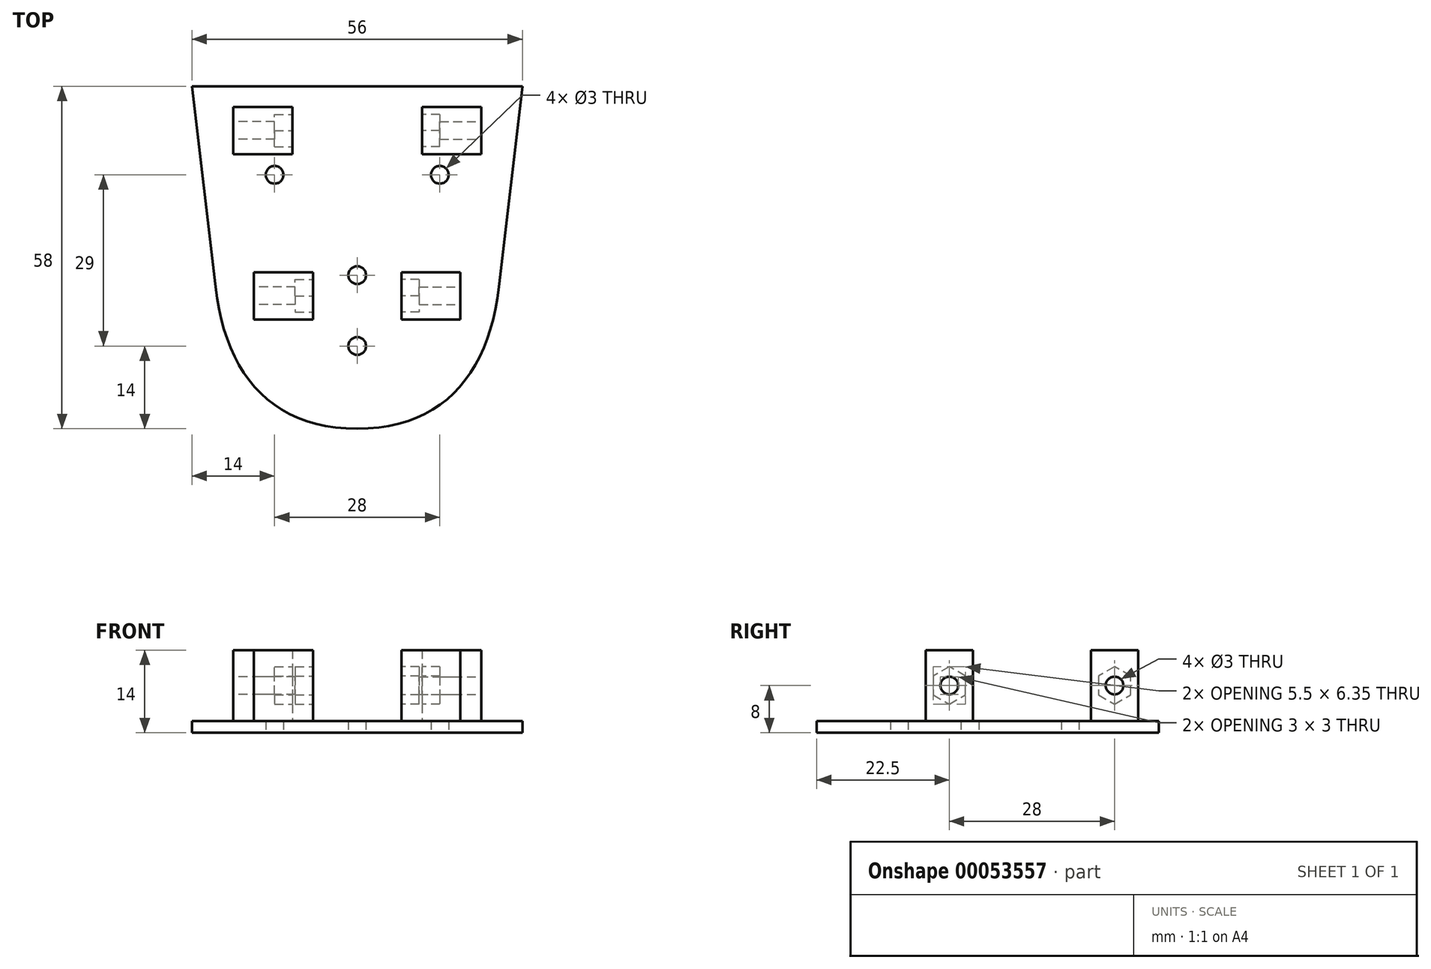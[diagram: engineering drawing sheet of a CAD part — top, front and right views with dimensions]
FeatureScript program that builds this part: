
annotation { "Feature Type Name" : "Feature", "Feature Type Description" : "" }
export const myFeature = defineFeature(function(context is Context, id is Id, definition is map)
    precondition{}
    {
        {
            var Q0;
            Q0=qCreatedBy(makeId("Top.planeOp"),FACE);
            var sketch = newSketch(context, id + "F0", { "sketchPlane" : qUnion([Q0])});
            skLineSegment(sketch, "E0.bottom", {"start": v(28, -29) * mm, "end": v(-28, -29) * mm, "construction": true});
            skLineSegment(sketch, "E0.top", {"start": v(28, 29) * mm, "end": v(-28, 29) * mm, "construction": true});
            skLineSegment(sketch, "E0.left", {"start": v(28, -29) * mm, "end": v(28, 29) * mm, "construction": true});
            skLineSegment(sketch, "E0.right", {"start": v(-28, -29) * mm, "end": v(-28, 29) * mm, "construction": true});
            skPoint(sketch, "E0.middle", {"position": v(0, 0) * mm});
            skLineSegment(sketch, "E1", {"start": v(-28, 14) * mm, "end": v(28, 14) * mm, "construction": true});
            skCircle(sketch, "E2", {"center": v(14, 14) * mm, "radius": 1.5 * mm});
            skCircle(sketch, "E3.MirrorC", {"center": v(-14, 14) * mm, "radius": 1.5 * mm});
            skCircle(sketch, "E4", {"center": v(0, -3) * mm, "radius": 1.5 * mm});
            skCircle(sketch, "E5", {"center": v(0, -15) * mm, "radius": 1.5 * mm});
            skLineSegment(sketch, "E6", {"start": v(-28, -5) * mm, "end": v(28, -5) * mm, "construction": true});
            skPoint(sketch, "E7", {"position": v(24, -5) * mm});
            skPoint(sketch, "E8.MirrorP", {"position": v(-24, -5) * mm});
            skLineSegment(sketch, "E9", {"start": v(28, 29) * mm, "end": v(24, -5) * mm});
            skFitSpline(sketch, "E10", {"points": [v(24, -5) * mm, v(0, -29) * mm], "startDerivative": vector(-5.06, -43.9) * mm, "endDerivative": vector(-43.96, 0) * mm});
            skFitSpline(sketch, "E11.MirrorCS", {"points": [v(-24, -5) * mm, v(0, -29) * mm], "startDerivative": vector(5.06, -43.9) * mm, "endDerivative": vector(43.96, 0) * mm});
            skLineSegment(sketch, "E12.MirrorCS", {"start": v(-28, 29) * mm, "end": v(-24, -5) * mm});
            skLineSegment(sketch, "E13", {"start": v(-28, 29) * mm, "end": v(28, 29) * mm});
            skSolve(sketch);
        }
        {
            var Q0;
            Q0 = qSketchRegion(id + "F0", true);
            extrude(context, id + "F1", {"entities" : qUnion([Q0]), "depth" : 2 * mm});
        }
        {
            var Q0;
            Q0=makeQuery(id+"F1.opExtrude","CAP_FACE",FACE,{"disambiguationData":[OSD([sQuery(id+"F0.wireOp",EDGE,"E2"),sQuery(id+"F0.wireOp",EDGE,"E3.MirrorC"),sQuery(id+"F0.wireOp",EDGE,"E4"),sQuery(id+"F0.wireOp",EDGE,"E5"),sQuery(id+"F0.wireOp",EDGE,"E9"),sQuery(id+"F0.wireOp",EDGE,"E10"),sQuery(id+"F0.wireOp",EDGE,"E11.MirrorCS"),sQuery(id+"F0.wireOp",EDGE,"E12.MirrorCS"),sQuery(id+"F0.wireOp",EDGE,"E13")])],"isStart":false});
            var sketch = newSketch(context, id + "F2", { "sketchPlane" : qUnion([Q0])});
            skLineSegment(sketch, "E14", {"start": v(-27.59, 25.5) * mm, "end": v(-21, 25.5) * mm, "construction": true});
            skLineSegment(sketch, "E15", {"start": v(21, 25.5) * mm, "end": v(21, -43.4) * mm, "construction": true});
            skLineSegment(sketch, "E16.bottom", {"start": v(11, 25.5) * mm, "end": v(21, 25.5) * mm});
            skLineSegment(sketch, "E16.top", {"start": v(11, 17.5) * mm, "end": v(21, 17.5) * mm});
            skLineSegment(sketch, "E16.left", {"start": v(11, 25.5) * mm, "end": v(11, 17.5) * mm});
            skLineSegment(sketch, "E16.right", {"start": v(21, 25.5) * mm, "end": v(21, 17.5) * mm});
            skLineSegment(sketch, "E17", {"start": v(17.5, -30.53) * mm, "end": v(17.5, 35.38) * mm, "construction": true});
            skLineSegment(sketch, "E18", {"start": v(11, 21.5) * mm, "end": v(21, 21.5) * mm, "construction": true});
            skLineSegment(sketch, "E19", {"start": v(17.5, -6.5) * mm, "end": v(3.5, -6.5) * mm, "construction": true});
            skLineSegment(sketch, "E20.top", {"start": v(17.5, -10.5) * mm, "end": v(7.5, -10.5) * mm});
            skLineSegment(sketch, "E20.left", {"start": v(17.5, -6.5) * mm, "end": v(17.5, -10.5) * mm});
            skLineSegment(sketch, "E20.right", {"start": v(7.5, -6.5) * mm, "end": v(7.5, -10.5) * mm});
            skLineSegment(sketch, "E21.MirrorCS", {"start": v(17.5, -2.5) * mm, "end": v(7.5, -2.5) * mm});
            skLineSegment(sketch, "E22.MirrorCS", {"start": v(7.5, -6.5) * mm, "end": v(7.5, -2.5) * mm});
            skLineSegment(sketch, "E23.MirrorCS", {"start": v(17.5, -6.5) * mm, "end": v(17.5, -2.5) * mm});
            skLineSegment(sketch, "E24.trimOffspring", {"start": v(-11, 25.5) * mm, "end": v(27.59, 25.5) * mm, "construction": true});
            skSolve(sketch);
        }
        {
            var Q0;
            Q0 = qSketchRegion(id + "F2", true);
            extrude(context, id + "F3", {"entities" : qUnion([Q0]), "depth" : 12 * mm});
        }
        {
            var Q0;
            Q0=makeQuery(id+"F3.opExtrude","SWEPT_FACE",FACE,{"disambiguationData":[OSD([sQuery(id+"F2.wireOp",EDGE,"E16.right")])]});
            var sketch = newSketch(context, id + "F4", { "sketchPlane" : qUnion([Q0])});
            skLineSegment(sketch, "E25", {"start": v(17.5, 8) * mm, "end": v(25.5, 8) * mm, "construction": true});
            skCircle(sketch, "E26", {"center": v(21.5, 8) * mm, "radius": 1.5 * mm});
            skSolve(sketch);
        }
        {
            var Q0;
            Q0 = qSketchRegion(id + "F4", true);
            extrude(context, id + "F5", {"entities" : qUnion([Q0]), "operationType" : NewBodyOperationType.REMOVE, "endBound" : BoundingType.UP_TO_NEXT, "oppositeDirection" : true, "depth" : 25 * mm});
        }
        {
            var Q0;
            Q0=makeQuery(id+"F3.opExtrude","SWEPT_FACE",FACE,{"disambiguationData":[OSD([sQuery(id+"F2.wireOp",EDGE,"E20.left"),sQuery(id+"F2.wireOp",EDGE,"E23.MirrorCS")])]});
            var sketch = newSketch(context, id + "F6", { "sketchPlane" : qUnion([Q0])});
            skLineSegment(sketch, "E27", {"start": v(-2.5, 8) * mm, "end": v(-10.5, 8) * mm, "construction": true});
            skCircle(sketch, "E28", {"center": v(-6.5, 8) * mm, "radius": 1.5 * mm});
            skSolve(sketch);
        }
        {
            var Q0;
            Q0 = qSketchRegion(id + "F6", true);
            extrude(context, id + "F7", {"entities" : qUnion([Q0]), "operationType" : NewBodyOperationType.REMOVE, "endBound" : BoundingType.UP_TO_NEXT, "oppositeDirection" : true, "depth" : 25 * mm});
        }
        {
            var Q0;
            Q0=makeQuery(id+"F3.opExtrude","SWEPT_FACE",FACE,{"disambiguationData":[OSD([sQuery(id+"F2.wireOp",EDGE,"E16.left")])]});
            var sketch = newSketch(context, id + "F8", { "sketchPlane" : qUnion([Q0])});
            skCircle(sketch, "E29.cCircle", {"center": v(-21.5, 8) * mm, "radius": 2.75 * mm, "construction": true});
            skLineSegment(sketch, "E29.0", {"start": v(-18.75, 6.41) * mm, "end": v(-21.5, 4.82) * mm});
            skLineSegment(sketch, "E29.1", {"start": v(-21.5, 4.82) * mm, "end": v(-24.25, 6.41) * mm});
            skLineSegment(sketch, "E29.2", {"start": v(-24.25, 6.41) * mm, "end": v(-24.25, 9.59) * mm});
            skLineSegment(sketch, "E29.3", {"start": v(-24.25, 9.59) * mm, "end": v(-21.5, 11.18) * mm});
            skLineSegment(sketch, "E29.4", {"start": v(-21.5, 11.18) * mm, "end": v(-18.75, 9.59) * mm});
            skLineSegment(sketch, "E29.5", {"start": v(-18.75, 9.59) * mm, "end": v(-18.75, 6.41) * mm});
            skPoint(sketch, "E29.0.midPoint", {"position": v(-20.13, 5.62) * mm});
            skLineSegment(sketch, "E30", {"start": v(-21.5, 8) * mm, "end": v(-21.5, 14.66) * mm, "construction": true});
            skPoint(sketch, "E30.endSnap0", {"position": v(-21.5, 14) * mm});
            skSolve(sketch);
        }
        {
            var Q0;
            Q0 = qSketchRegion(id + "F8", true);
            extrude(context, id + "F9", {"entities" : qUnion([Q0]), "operationType" : NewBodyOperationType.REMOVE, "oppositeDirection" : true, "depth" : 3 * mm});
        }
        {
            var Q0;
            Q0=makeQuery(id+"F3.opExtrude","SWEPT_BODY",BODY,{"disambiguationData":[OSD([sQuery(id+"F2.wireOp",EDGE,"E16.bottom"),sQuery(id+"F2.wireOp",EDGE,"E16.top"),sQuery(id+"F2.wireOp",EDGE,"E16.left"),sQuery(id+"F2.wireOp",EDGE,"E16.right")])]});
            var Q1;
            Q1=qCreatedBy(makeId("Right.planeOp"),FACE);
            mirror(context, id + "F10", {"operationType" : NewBodyOperationType.ADD, "entities" : qUnion([Q0]), "mirrorPlane" : qUnion([Q1])});
        }
        {
            var Q0;
            Q0=makeQuery(id+"F3.opExtrude","SWEPT_FACE",FACE,{"disambiguationData":[OSD([sQuery(id+"F2.wireOp",EDGE,"E20.right"),sQuery(id+"F2.wireOp",EDGE,"E22.MirrorCS")])]});
            var sketch = newSketch(context, id + "F11", { "sketchPlane" : qUnion([Q0])});
            skLineSegment(sketch, "E31", {"start": v(6.5, 8) * mm, "end": v(6.5, 14) * mm, "construction": true});
            skCircle(sketch, "E32.cCircle", {"center": v(6.5, 8) * mm, "radius": 2.75 * mm, "construction": true});
            skLineSegment(sketch, "E32.0", {"start": v(6.5, 11.18) * mm, "end": v(9.25, 9.59) * mm});
            skLineSegment(sketch, "E32.1", {"start": v(9.25, 9.59) * mm, "end": v(9.25, 6.41) * mm});
            skLineSegment(sketch, "E32.2", {"start": v(9.25, 6.41) * mm, "end": v(6.5, 4.82) * mm});
            skLineSegment(sketch, "E32.3", {"start": v(6.5, 4.82) * mm, "end": v(3.75, 6.41) * mm});
            skLineSegment(sketch, "E32.4", {"start": v(3.75, 6.41) * mm, "end": v(3.75, 9.59) * mm});
            skLineSegment(sketch, "E32.5", {"start": v(3.75, 9.59) * mm, "end": v(6.5, 11.18) * mm});
            skPoint(sketch, "E32.0.midPoint", {"position": v(7.88, 10.38) * mm});
            skSolve(sketch);
        }
        {
            var Q0;
            Q0 = qSketchRegion(id + "F11", true);
            extrude(context, id + "F12", {"entities" : qUnion([Q0]), "operationType" : NewBodyOperationType.REMOVE, "oppositeDirection" : true, "depth" : 3 * mm});
        }
        {
            var Q0;
            Q0=makeQuery(id+"F3.opExtrude","SWEPT_BODY",BODY,{"disambiguationData":[OSD([sQuery(id+"F2.wireOp",EDGE,"E20.top"),sQuery(id+"F2.wireOp",EDGE,"E20.left"),sQuery(id+"F2.wireOp",EDGE,"E20.right"),sQuery(id+"F2.wireOp",EDGE,"E21.MirrorCS"),sQuery(id+"F2.wireOp",EDGE,"E22.MirrorCS"),sQuery(id+"F2.wireOp",EDGE,"E23.MirrorCS")])]});
            var Q1;
            Q1=qCreatedBy(makeId("Right.planeOp"),FACE);
            mirror(context, id + "F13", {"operationType" : NewBodyOperationType.ADD, "entities" : qUnion([Q0]), "mirrorPlane" : qUnion([Q1])});
        }
    });
